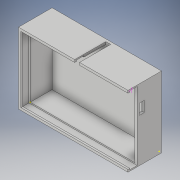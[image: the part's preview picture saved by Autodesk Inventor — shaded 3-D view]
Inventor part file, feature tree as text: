
AUTODESK INVENTOR PART (.ipt)
format: ipt  version: 2018.3 (Build 223284000, 284)  size: 147,456 bytes
history: native  units: in
note: dims shown in document units (in); Inventor stores cm internally (conversion verified against a paired STEP export)
features: sketch x8, extrude x5, shell x1
ambient origin geometry x8: Origin, YZ Plane, XZ Plane, XY Plane, X Axis, Y Axis, Z Axis, Center Point
bodies: Solid1 (feature_tree)
feature tree (14):
  extrude  "Extrusion1"  Depth=2.0866in
  shell  "Shell1"  Thickness=0.9842in
  sketch  "Sketch2"  dims[d4=0.078in d5=0.157in]
  extrude  "Extrusion2"  Depth=0.157in
  extrude  "Extrusion3"  Depth=0.335in TaperAngle=0.0deg
  sketch  "Sketch5"  dims[d14=0.079in d15=0.0in d16=1.0in d17=0.0in]
  sketch  "Sketch6"
  extrude  "Extrusion4"  Depth=3.4252in TaperAngle=0.0deg
  extrude  "Extrusion5"  Depth=1.0in TaperAngle=0.0deg
  sketch  "Sketch1"  dims[d0=3.307in d1=2.0866in d2=0.9842in d3=0.0in]
  sketch  "Sketch3"  dims[d6=0.335in d7=0.9055in d8=0.0in]
  sketch  "Sketch4"  dims[d9=0.1969in d11=3.4252in d12=0.0in]
  sketch  "Sketch7"
  sketch  "Sketch8"
